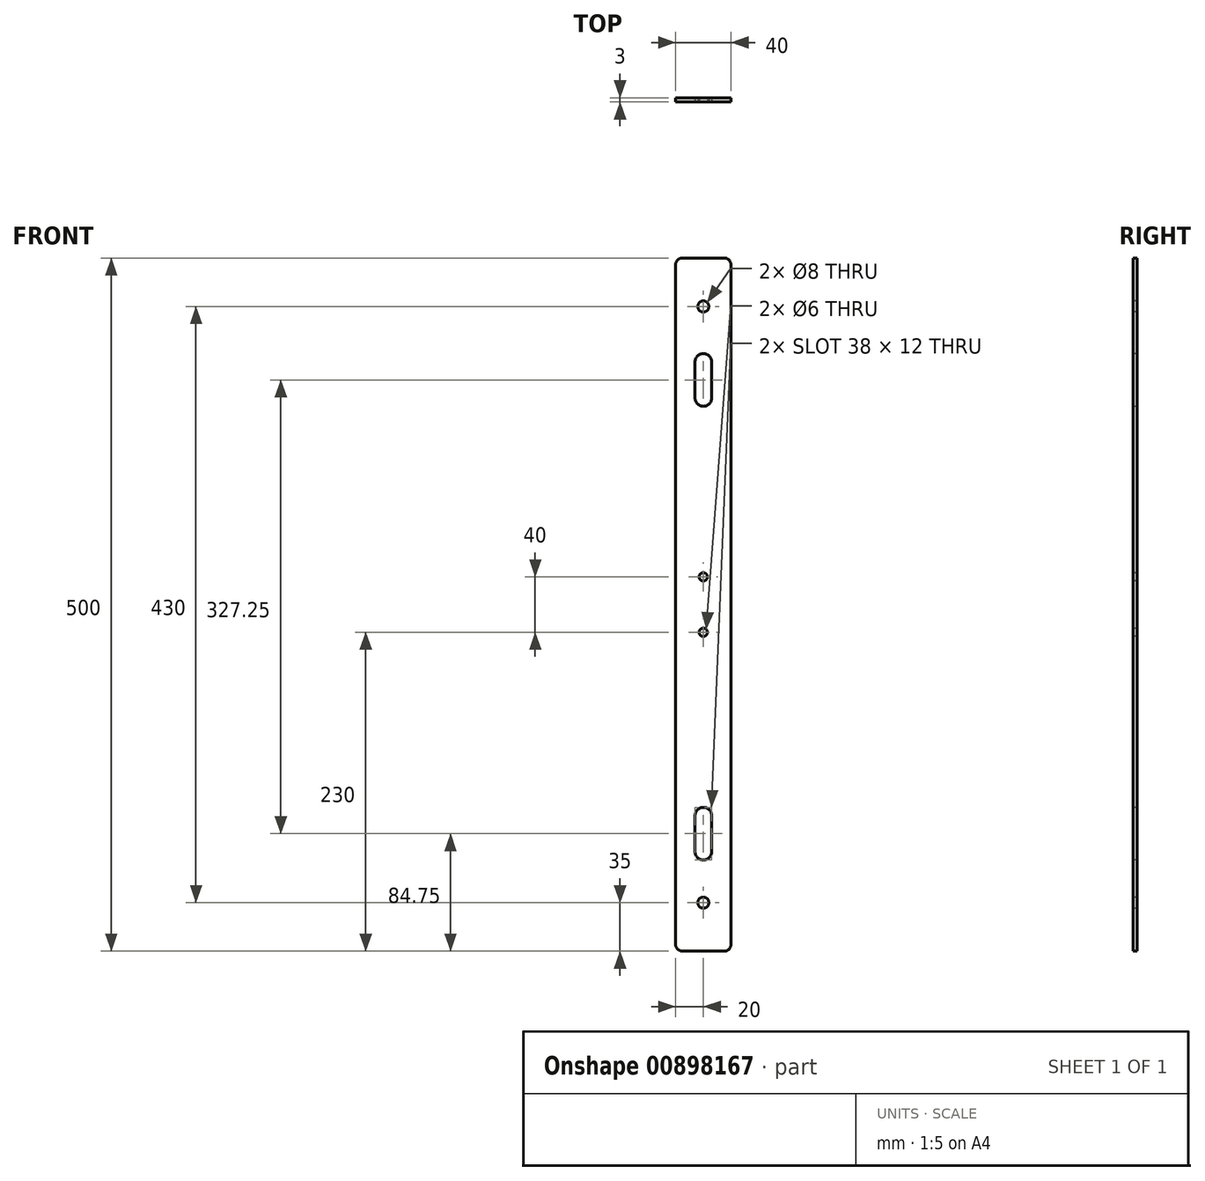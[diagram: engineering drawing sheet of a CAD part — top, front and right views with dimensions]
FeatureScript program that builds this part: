
annotation { "Feature Type Name" : "Feature", "Feature Type Description" : "" }
export const myFeature = defineFeature(function(context is Context, id is Id, definition is map)
    precondition{}
    {
        {
            var Q0;
            Q0=qCreatedBy(makeId("Front.planeOp"),FACE);
            var sketch = newSketch(context, id + "F0", { "sketchPlane" : qUnion([Q0])});
            skLineSegment(sketch, "E0.bottom", {"start": v(-20, 250) * mm, "end": v(20, 250) * mm});
            skLineSegment(sketch, "E0.top", {"start": v(-20, -250) * mm, "end": v(20, -250) * mm});
            skLineSegment(sketch, "E0.left", {"start": v(-20, 250) * mm, "end": v(-20, -250) * mm});
            skLineSegment(sketch, "E0.right", {"start": v(20, 250) * mm, "end": v(20, -250) * mm});
            skPoint(sketch, "E0.middle", {"position": v(0, 0) * mm});
            skSolve(sketch);
        }
        {
            var Q0;
            Q0=qSketchRegion(id+"F0",true);
            extrude(context, id + "F1", {"entities" : qUnion([Q0]), "depth" : 3 * mm, "offsetDistance" : 25 * mm});
        }
        {
            var Q0;
            Q0=makeQuery(id+"F1.opExtrude","CAP_FACE",FACE,{"disambiguationData":[OSD([sQuery(id+"F0.wireOp",EDGE,"E0.bottom"),sQuery(id+"F0.wireOp",EDGE,"E0.top"),sQuery(id+"F0.wireOp",EDGE,"E0.left"),sQuery(id+"F0.wireOp",EDGE,"E0.right")])],"isStart":false});
            var sketch = newSketch(context, id + "F2", { "sketchPlane" : qUnion([Q0])});
            skPoint(sketch, "E1", {"position": v(0, 215) * mm});
            skPoint(sketch, "E2.MirrorP", {"position": v(0, -215) * mm});
            skSolve(sketch);
        }
        {
            var Q0;
            Q0=sQuery(id+"F2.wireOp",VERTEX,"E2.MirrorP");
            var Q1;
            Q1=sQuery(id+"F2.wireOp",VERTEX,"E1");
            var Q2;
            Q2=makeQuery(id+"F1.opExtrude","SWEPT_BODY",BODY,{"disambiguationData":[OSD([sQuery(id+"F0.wireOp",EDGE,"E0.bottom"),sQuery(id+"F0.wireOp",EDGE,"E0.top"),sQuery(id+"F0.wireOp",EDGE,"E0.left"),sQuery(id+"F0.wireOp",EDGE,"E0.right")])]});
            hole(context, id + "F3", {"style" : HoleStyle.SIMPLE, "endStyle" : HoleEndStyle.THROUGH, "holeDiameter" : 8 * mm, "majorDiameter" : 5 * mm, "isTappedThrough" : true, "tappedDepth" : 12 * mm, "tapClearance" : 3, "startFromSketch" : true, "locations" : qUnion([Q0, Q1]), "scope" : qUnion([Q2])});
        }
        {
            var Q0;
            Q0=makeQuery(id+"F1.opExtrude","CAP_FACE",FACE,{"disambiguationData":[OSD([sQuery(id+"F0.wireOp",EDGE,"E0.bottom"),sQuery(id+"F0.wireOp",EDGE,"E0.top"),sQuery(id+"F0.wireOp",EDGE,"E0.left"),sQuery(id+"F0.wireOp",EDGE,"E0.right")])],"isStart":false});
            var sketch = newSketch(context, id + "F4", { "sketchPlane" : qUnion([Q0])});
            skPoint(sketch, "E3", {"position": v(0, 149) * mm});
            skSolve(sketch);
        }
        {
            var Q0;
            Q0=sQuery(id+"F4.wireOp",VERTEX,"E3");
            var Q1;
            Q1=makeQuery(id+"F1.opExtrude","SWEPT_BODY",BODY,{"disambiguationData":[OSD([sQuery(id+"F0.wireOp",EDGE,"E0.bottom"),sQuery(id+"F0.wireOp",EDGE,"E0.top"),sQuery(id+"F0.wireOp",EDGE,"E0.left"),sQuery(id+"F0.wireOp",EDGE,"E0.right")])]});
            hole(context, id + "F5", {"style" : HoleStyle.SIMPLE, "endStyle" : HoleEndStyle.THROUGH, "holeDiameter" : 12 * mm, "majorDiameter" : 5 * mm, "isTappedThrough" : true, "tappedDepth" : 12 * mm, "tapClearance" : 3, "startFromSketch" : true, "locations" : qUnion([Q0]), "scope" : qUnion([Q1])});
        }
        {
            var Q0;
            Q0=makeQuery(id+"F1.opExtrude","CAP_FACE",FACE,{"disambiguationData":[OSD([sQuery(id+"F0.wireOp",EDGE,"E0.bottom"),sQuery(id+"F0.wireOp",EDGE,"E0.top"),sQuery(id+"F0.wireOp",EDGE,"E0.left"),sQuery(id+"F0.wireOp",EDGE,"E0.right")])],"isStart":false});
            var sketch = newSketch(context, id + "F6", { "sketchPlane" : qUnion([Q0])});
            skPoint(sketch, "E4", {"position": v(0, 215) * mm});
            skPoint(sketch, "E5.MirrorP", {"position": v(0, -215) * mm});
            skLineSegment(sketch, "E6", {"start": v(0, 155) * mm, "end": v(0, 175) * mm});
            skArc(sketch, "E7.0.startCap", {"start": v(3, 155) * mm, "mid": v(0, 152) * mm, "end": v(-3, 155) * mm});
            skArc(sketch, "E7.0.endCap", {"start": v(-3, 175) * mm, "mid": v(0, 178) * mm, "end": v(3, 175) * mm});
            skLineSegment(sketch, "E7.0.left", {"start": v(-3, 155) * mm, "end": v(-3, 175) * mm});
            skLineSegment(sketch, "E7.0.right", {"start": v(3, 155) * mm, "end": v(3, 175) * mm});
            skPoint(sketch, "E8", {"position": v(0, -178.25) * mm});
            skSolve(sketch);
        }
        {
            var Q0;
            Q0=qSketchRegion(id+"F6",true);
            extrude(context, id + "F7", {"entities" : qUnion([Q0]), "operationType" : NewBodyOperationType.REMOVE, "oppositeDirection" : true, "depth" : 6 * mm, "offsetDistance" : 25 * mm});
        }
        {
            var Q0;
            Q0=sQuery(id+"F6.wireOp",VERTEX,"E8");
            var Q1;
            Q1=makeQuery(id+"F1.opExtrude","SWEPT_BODY",BODY,{"disambiguationData":[OSD([sQuery(id+"F0.wireOp",EDGE,"E0.bottom"),sQuery(id+"F0.wireOp",EDGE,"E0.top"),sQuery(id+"F0.wireOp",EDGE,"E0.left"),sQuery(id+"F0.wireOp",EDGE,"E0.right")])]});
            hole(context, id + "F8", {"style" : HoleStyle.SIMPLE, "endStyle" : HoleEndStyle.THROUGH, "holeDiameter" : 12 * mm, "majorDiameter" : 5 * mm, "isTappedThrough" : true, "tappedDepth" : 12 * mm, "tapClearance" : 3, "startFromSketch" : true, "locations" : qUnion([Q0]), "scope" : qUnion([Q1])});
        }
        {
            var Q0;
            Q0=makeQuery(id+"F1.opExtrude","CAP_FACE",FACE,{"disambiguationData":[OSD([sQuery(id+"F0.wireOp",EDGE,"E0.bottom"),sQuery(id+"F0.wireOp",EDGE,"E0.top"),sQuery(id+"F0.wireOp",EDGE,"E0.left"),sQuery(id+"F0.wireOp",EDGE,"E0.right")])],"isStart":false});
            var sketch = newSketch(context, id + "F9", { "sketchPlane" : qUnion([Q0])});
            skLineSegment(sketch, "E9", {"start": v(0, -172.25) * mm, "end": v(0, -152.25) * mm});
            skArc(sketch, "E10.0.startCap", {"start": v(3, -172.25) * mm, "mid": v(0, -175.25) * mm, "end": v(-3, -172.25) * mm});
            skArc(sketch, "E10.0.endCap", {"start": v(-3, -152.25) * mm, "mid": v(0, -149.25) * mm, "end": v(3, -152.25) * mm});
            skLineSegment(sketch, "E10.0.left", {"start": v(-3, -172.25) * mm, "end": v(-3, -152.25) * mm});
            skLineSegment(sketch, "E10.0.right", {"start": v(3, -172.25) * mm, "end": v(3, -152.25) * mm});
            skSolve(sketch);
        }
        {
            var Q0;
            Q0=qSketchRegion(id+"F9",true);
            extrude(context, id + "F10", {"entities" : qUnion([Q0]), "operationType" : NewBodyOperationType.REMOVE, "oppositeDirection" : true, "depth" : 6 * mm, "offsetDistance" : 25 * mm});
        }
        {
            var Q0;
            Q0=makeQuery(id+"F1.opExtrude","CAP_FACE",FACE,{"disambiguationData":[OSD([sQuery(id+"F0.wireOp",EDGE,"E0.bottom"),sQuery(id+"F0.wireOp",EDGE,"E0.top"),sQuery(id+"F0.wireOp",EDGE,"E0.left"),sQuery(id+"F0.wireOp",EDGE,"E0.right")])],"isStart":false});
            var sketch = newSketch(context, id + "F11", { "sketchPlane" : qUnion([Q0])});
            skLineSegment(sketch, "E11", {"start": v(0, 149) * mm, "end": v(0, 175) * mm});
            skArc(sketch, "E12.0.startCap", {"start": v(6, 149) * mm, "mid": v(0, 143) * mm, "end": v(-6, 149) * mm});
            skArc(sketch, "E12.0.endCap", {"start": v(-6, 175) * mm, "mid": v(0, 181) * mm, "end": v(6, 175) * mm});
            skLineSegment(sketch, "E12.0.left", {"start": v(-6, 149) * mm, "end": v(-6, 175) * mm});
            skLineSegment(sketch, "E12.0.right", {"start": v(6, 149) * mm, "end": v(6, 175) * mm});
            skLineSegment(sketch, "E13", {"start": v(0, -178.25) * mm, "end": v(0, -152.25) * mm});
            skArc(sketch, "E14.0.startCap", {"start": v(6, -178.25) * mm, "mid": v(0, -184.25) * mm, "end": v(-6, -178.25) * mm});
            skArc(sketch, "E14.0.endCap", {"start": v(-6, -152.25) * mm, "mid": v(0, -146.25) * mm, "end": v(6, -152.25) * mm});
            skLineSegment(sketch, "E14.0.left", {"start": v(-6, -178.25) * mm, "end": v(-6, -152.25) * mm});
            skLineSegment(sketch, "E14.0.right", {"start": v(6, -178.25) * mm, "end": v(6, -152.25) * mm});
            skSolve(sketch);
        }
        {
            var Q0;
            Q0 = qSketchRegion(id + "F11", true);
            extrude(context, id + "F12", {"entities" : qUnion([Q0]), "operationType" : NewBodyOperationType.REMOVE, "oppositeDirection" : true, "depth" : 6 * mm, "offsetDistance" : 25 * mm});
        }
        {
            var Q0;
            Q0=makeQuery(id+"F1.opExtrude","SWEPT_EDGE",EDGE,{"disambiguationData":[OSD([sQuery(id+"F0.wireOp",EDGE,"E0.bottom"),sQuery(id+"F0.wireOp",EDGE,"E0.right")])]});
            var Q1;
            Q1=makeQuery(id+"F1.opExtrude","SWEPT_EDGE",EDGE,{"disambiguationData":[OSD([sQuery(id+"F0.wireOp",EDGE,"E0.bottom"),sQuery(id+"F0.wireOp",EDGE,"E0.left")])]});
            var Q2;
            Q2=makeQuery(id+"F1.opExtrude","SWEPT_EDGE",EDGE,{"disambiguationData":[OSD([sQuery(id+"F0.wireOp",EDGE,"E0.top"),sQuery(id+"F0.wireOp",EDGE,"E0.right")])]});
            var Q3;
            Q3=makeQuery(id+"F1.opExtrude","SWEPT_EDGE",EDGE,{"disambiguationData":[OSD([sQuery(id+"F0.wireOp",EDGE,"E0.top"),sQuery(id+"F0.wireOp",EDGE,"E0.left")])]});
            fillet(context, id + "F13", {"entities" : qUnion([Q0, Q1, Q2, Q3]), "radius" : 5 * mm, "tangentPropagation" : true, "allowEdgeOverflow" : false});
        }
        {
            var Q0;
            Q0=makeQuery(id+"F1.opExtrude","CAP_FACE",FACE,{"disambiguationData":[OSD([sQuery(id+"F0.wireOp",EDGE,"E0.bottom"),sQuery(id+"F0.wireOp",EDGE,"E0.top"),sQuery(id+"F0.wireOp",EDGE,"E0.left"),sQuery(id+"F0.wireOp",EDGE,"E0.right")])],"isStart":false});
            var sketch = newSketch(context, id + "F14", { "sketchPlane" : qUnion([Q0])});
            skPoint(sketch, "E15", {"position": v(0, 20) * mm});
            skPoint(sketch, "E15.positionSnap0", {"position": v(0, 181) * mm});
            skPoint(sketch, "E16.MirrorP", {"position": v(0, -20) * mm});
            skSolve(sketch);
        }
        {
            var Q0;
            Q0=sQuery(id+"F14.wireOp",VERTEX,"E15");
            var Q1;
            Q1=sQuery(id+"F14.wireOp",VERTEX,"E16.MirrorP");
            var Q2;
            Q2=makeQuery(id+"F1.opExtrude","SWEPT_BODY",BODY,{"disambiguationData":[OSD([sQuery(id+"F0.wireOp",EDGE,"E0.bottom"),sQuery(id+"F0.wireOp",EDGE,"E0.top"),sQuery(id+"F0.wireOp",EDGE,"E0.left"),sQuery(id+"F0.wireOp",EDGE,"E0.right")])]});
            hole(context, id + "F15", {"style" : HoleStyle.SIMPLE, "endStyle" : HoleEndStyle.THROUGH, "holeDiameter" : 6 * mm, "majorDiameter" : 5 * mm, "isTappedThrough" : true, "tappedDepth" : 12 * mm, "tapClearance" : 3, "startFromSketch" : true, "locations" : qUnion([Q0, Q1]), "scope" : qUnion([Q2])});
        }
    });
